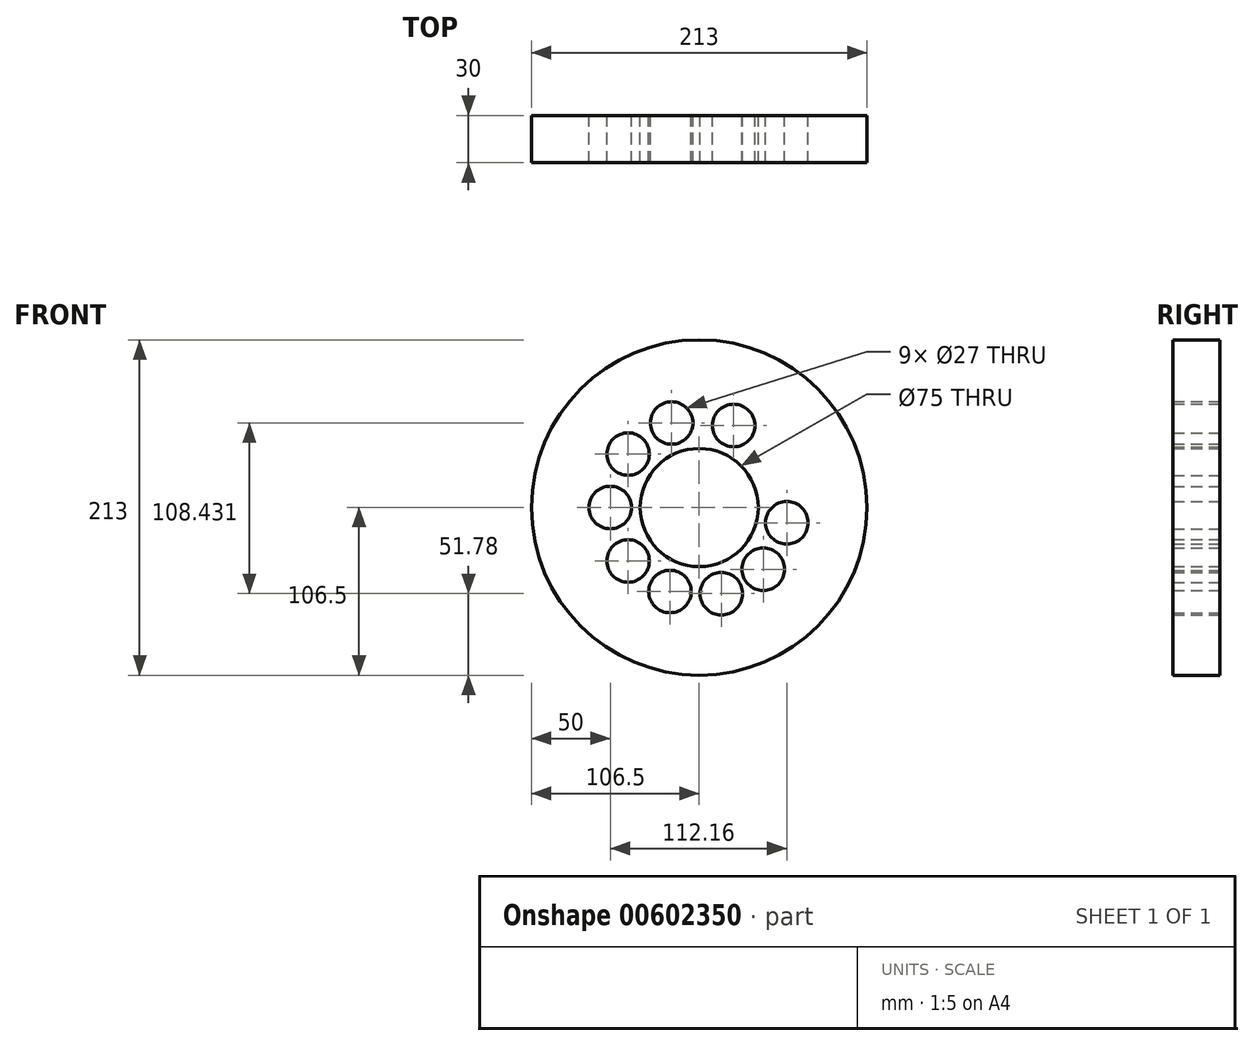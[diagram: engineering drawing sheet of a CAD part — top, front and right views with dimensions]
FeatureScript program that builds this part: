
annotation { "Feature Type Name" : "Feature", "Feature Type Description" : "" }
export const myFeature = defineFeature(function(context is Context, id is Id, definition is map)
    precondition{}
    {
        {
            var Q0;
            Q0=qCreatedBy(makeId("Front.planeOp"),FACE);
            var sketch = newSketch(context, id + "F0", { "sketchPlane" : qUnion([Q0])});
            skCircle(sketch, "E0", {"center": v(0, 0) * mm, "radius": 32.5 * mm});
            skCircle(sketch, "E1", {"center": v(0, 0) * mm, "radius": 37.5 * mm});
            skCircle(sketch, "E2", {"center": v(0, 0) * mm, "radius": 75 * mm});
            skCircle(sketch, "E3", {"center": v(0, 0) * mm, "radius": 106.5 * mm});
            skCircle(sketch, "E4", {"center": v(21.85, 52.1) * mm, "radius": 13.5 * mm});
            skCircle(sketch, "E5", {"center": v(-17.53, 53.71) * mm, "radius": 13.5 * mm});
            skCircle(sketch, "E6", {"center": v(-45.17, 33.95) * mm, "radius": 13.5 * mm});
            skCircle(sketch, "E7", {"center": v(-56.5, 0) * mm, "radius": 13.5 * mm});
            skCircle(sketch, "E8", {"center": v(-45.17, -33.95) * mm, "radius": 13.5 * mm});
            skCircle(sketch, "E9", {"center": v(-18.56, -53.37) * mm, "radius": 13.5 * mm});
            skCircle(sketch, "E10", {"center": v(14.07, -54.72) * mm, "radius": 13.5 * mm});
            skCircle(sketch, "E11", {"center": v(40.7, -39.18) * mm, "radius": 13.5 * mm});
            skCircle(sketch, "E12", {"center": v(55.66, -9.7) * mm, "radius": 13.5 * mm});
            skArc(sketch, "E13.trimOffspring", {"start": v(26.65, -49.82) * mm, "mid": v(28.47, -48.8) * mm, "end": v(30.25, -47.72) * mm});
            skSolve(sketch);
        }
        {
            var Q0;
            Q0 = qSketchRegion(id + "F0", true);
            var Q1;
            Q1=makeQuery(id+"F0.imprint","IMPRINT",FACE,{"disambiguationData":[TD([[makeQuery(id+"F0.imprint","IMPRINT",EDGE,{"derivedFrom":sQuery(id+"F0.wireOp",EDGE,"E1")}),-1.0]])]});
            extrude(context, id + "F1", {"entities" : qUnion([Q0, Q1]), "depth" : 30 * mm, "offsetDistance" : 25 * mm});
        }
    });
